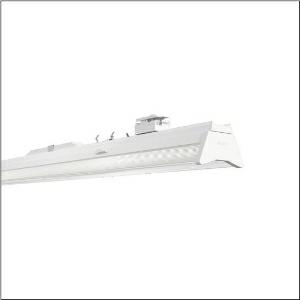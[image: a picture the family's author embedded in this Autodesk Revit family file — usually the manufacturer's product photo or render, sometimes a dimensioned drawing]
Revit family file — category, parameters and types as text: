
# Revit family: licross_11_performance_mo_51tm16cn49xg
name_source: partatom
category: Lighting Fixtures
units: mm (PartAtom-declared; Revit-internal decimal feet)

## family parameters
Cut with Voids When Loaded = No
Host = Face
Light Source = No
Part Type = Normal
Room Calculation Point = No
Round Connector Dimension = Use Diameter
Shared = No

## types (1)
- --- (1 x LED, 9190 lm, 49.4 W, 4000K)
    Apparent Load = 49 VA
    CIE Flux Codes = 66 88 96 79 100
    Color Rendering = 80
    Color Temperature = 4000K
    Default Elevation = 1800 mm
    Description = Licross 11 Performance MO, luminaire insert, of sheet steel, galvanised, coil coated, white, length: 1.500mm, width: 120mm, height: 123mm, LED rated luminous flux: 9.190lm, light colour: 840, SDCM (Standard Deviation of Colour Matching)MacAdam ≤ 2 SDCM (initial), control gear: ON/OFF Multilumen, CLOi, with plug, 3-pole, with phase selection, mains connection: 220..240V, AC, 50/60Hz, start of lifetime: 49W, end of service life: 55W, internal wiring halogen-free, primary light control with lens, of plastic, primary optical cover: cover, of PMMA, light emission: direct/indirect distribution, primary light characteristic: symmetric, protection rating (complete): IP40, insulation class (complete): insulation class I (protective earthing), certification: CE, ENEC, VDE, UKCA, protection symbol: D if used in an environment without relevant dust loads with corresponding accessories, impact resistance: IK06, permissible ambient temperature for indoor applications: -35..+40°C, corresponds to IFS (International Featured Standards) requirements for safety and quality in the food industry, reducing of maximum allowable ambient temperature of 5°C with ceiling mounting, LABS conformity tested according to VDMA 24364:2018-05, The light source and the operating device comply with the requirements of the Ecodesign Regulation (EU) 2019/2020 and are replaceable in accordance with this regulation, packaging unit: 1 piece
    Height = 114 mm
    Lamp = 1 x LED
    Lamp Light Flux = 9190 lm
    Lamp Power = 49.4 W
    Lamp count = 1
    Length = 1500 mm
    Luminous efficacy = 186 lm/W
    Manufacturer = Siteco
    ModVariant = No
    Model = 51TM16CN49XG
    Mounting Place = Ceiling
    Mounting Type = Pendant
    Number of Poles = 1
    OnlyDefault = Yes
    Power Factor = 1
    Product Name = Licross 11 Performance MO
    Product group = luminaire insert | ceiling pendant
    ProductGroupID = 901
    Protection Class = Protection class I
    Protection Degree = IP 40
    RLX_Detail_Level = 1
    RLX_Emergency_Light_Flux = 0 lm
    RLX_Emergency_Type = 0
    RLX_Emergency_Type_DB = No
    RlxData = <blob elided: 32077 chars, md5=d58ee4df>
    Socket = socket
    Standby Power = 0 W
    System Light Flux = 9190 lm
    System Power = 49 W
    Type Comments = factory setting: luminous flux: 100 % | (A | C | E) | 113 mA
    Type Image = l_1256138.jpg
    URL = http://relux.com
    VarID = @adj_091431
    Voltage = 0 V
    Weight = 0.00 kg
    Width = 120 mm

## geometry (parser evidence)
native form markers: Blend x4, Sweep x12
no freeform markers — native parametric forms only
